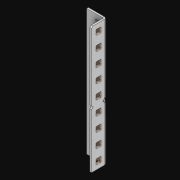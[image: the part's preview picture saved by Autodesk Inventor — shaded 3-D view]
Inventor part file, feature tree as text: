
AUTODESK INVENTOR PART (.ipt)
format: ipt  version: 2021 (Build 250183000, 183)  size: 1,099,264 bytes
history: native  units: in
note: dims shown in document units (in); Inventor stores cm internally (conversion verified against a paired STEP export)
features: extrude x20, other x18, sketch x4, pattern_linear x2, sheet_metal_op x1
ambient origin geometry x8: Origin, YZ Plane, XZ Plane, XY Plane, X Axis, Y Axis, Z Axis, Center Point
bodies: Solid1 (feature_tree)
feature tree (45):
  pattern_linear  "Rectangular Pattern1"  Spacing1=0.5in  [1 undecoded]
  pattern_linear  "Rectangular Pattern3"  Count1=9  [1 undecoded]
  extrude  "Extrusion1"  Depth=0.5in
  extrude  "Extrusion2"  Depth=0.5in
  sketch  "Sketch1"  dims[d0=0.182in]
  other  "Srf1"
  sketch  "Sketch3"  dims[d1=0.063in d2=0.0in]
  other  "Srf3"
  other  "Srf4"
  other  "Srf5"
  other  "Srf6"
  other  "Srf7"
  other  "Srf8"
  other  "Srf9"
  other  "Srf10"
  other  "Srf11"
  other  "Srf142"
  other  "Srf143"
  other  "Srf144"
  other  "Srf145"
  other  "Srf146"
  other  "Srf147"
  other  "Srf148"
  other  "Srf149"
  sketch  "Sketch4"  dims[d6=0.182in]
  sketch  "Sketch5"  dims[d7=0.063in d8=0.0in d11=0.5in d12=0.3937in d14=0.5in d18=3.5433in d20=0.5in d21=13.0in d22=0.0in d23=0.841in d24=0.0in]
  sheet_metal_op  "Fold1"
  extrude  "ExtrusionSrf1"  TaperAngle=0.0deg  [1 undecoded]
  extrude  "ExtrusionSrf3"  Depth=0.5in TaperAngle=0.0deg
  extrude  "ExtrusionSrf4"  [1 undecoded]
  extrude  "ExtrusionSrf5"  [1 undecoded]
  extrude  "ExtrusionSrf6"  [1 undecoded]
  extrude  "ExtrusionSrf7"  [1 undecoded]
  extrude  "ExtrusionSrf8"  [1 undecoded]
  extrude  "ExtrusionSrf9"  [1 undecoded]
  extrude  "ExtrusionSrf10"  [1 undecoded]
  extrude  "ExtrusionSrf11"  [1 undecoded]
  extrude  "ExtrusionSrf142"  [1 undecoded]
  extrude  "ExtrusionSrf143"  [1 undecoded]
  extrude  "ExtrusionSrf144"  [1 undecoded]
  extrude  "ExtrusionSrf145"  [1 undecoded]
  extrude  "ExtrusionSrf146"  [1 undecoded]
  extrude  "ExtrusionSrf147"  [1 undecoded]
  extrude  "ExtrusionSrf148"  [1 undecoded]
  extrude  "ExtrusionSrf149"  [1 undecoded]
note: 19 required parameter values undecoded (feature->parameter linkage not recoverable at this tier; creation-order binding heuristic only, values carry confidence <= 0.55)
